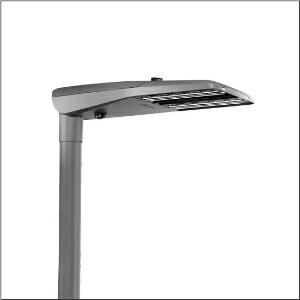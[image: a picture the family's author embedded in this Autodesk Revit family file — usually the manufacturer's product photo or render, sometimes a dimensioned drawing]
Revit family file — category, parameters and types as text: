
# Revit family: streetlight_sl_11_iq_midi___st1_2a_5xc3a11y08me_f942
name_source: partatom
category: Lighting Fixtures
units: mm (PartAtom-declared; Revit-internal decimal feet)

## family parameters
Cut with Voids When Loaded = No
Host = Face
Light Source = No
Part Type = Normal
Room Calculation Point = No
Round Connector Dimension = Use Diameter
Shared = No

## types (1)
- --- (1 x LED, 11200 lm, 123.4 W, 1800K)
    Apparent Load = 123 VA
    CIE Flux Codes = 32 70 96 100 100
    Color Rendering = 70
    Color Temperature = 1800K
    Default Elevation = 1800 mm  [stored 5.90551 ft]
    Description = Streetlight SL 11 iQ midi, mast luminaire, primary light control with 3 zone facetted reflector, of plastic, silver coated, highly specular, primary optical cover: cover, of PMMA, transparent, light distribution: ST1.2a, light emission: direct distribution, primary light characteristic: asymmetric, installation type: post-top, side-entry, LED, High Power LED, rated luminous flux: 11.200lm, luminous efficacy: 91lm/W, light colour: 718, colour temperature: 1800K, control: presetting dimming logarithmic, Street-Remote, Auto-Match, Temp-Guard, Lumen-Switch, Night-Set, Smart-Wire, Light-Fading, Desk-Remote (wireless, voltage-free reading and setting of iQ features in the workshop via application-optimized NFC function/RFID function), optimised constant luminous flux control (CLO 2.0), with cable H07RN-F 5x 1.5mm², mains connection: 230..240V, AC, 50/60Hz, connection cable pre-assembled, cable length: 12,5m, start of lifetime: 123W, end of service life: 131W, reduction: 54W, luminaire housing, of diecast aluminium, powder-coated, Siteco® metallic grey (DB 702S), please order mast flange separately, inclination adjustable without tools: 0°, 5°, 10°, 15° (post-top) | 0°, -5°, -10°, -15° (side-entry), sealing non-destructively replaceable, multi-level sealing system, length: 780mm, width: 376mm, height: 118mm, mast flange for spigot size: 42mm (side-entry): 5XC10008XM4, 60/48mm (side-entry/post-top): 5XC10108XM2, 76/60mm (side-entry/post-top): 5XC10108XM1, equipment: Power, Smart Interface below and above, protection rating (complete): IP66, insulation class (complete): insulation class II (safety insulation), certification: CE, ENEC, VDE, UKCA, impact resistance: IK09, permissible operating ambient temperature for outdoor applications: -25..+50°C, standard-compliant lighting for roads and squares, Environmental Product Declaration (EPD) tested and certified by an independent institute, packaging unit: 1 piece

Light Distribution: ST1.2a
    Height = 118 mm
    Lamp = 1 x LED
    Lamp Light Flux = 11200 lm
    Lamp Power = 123.4 W
    Lamp count = 1
    Length = 780 mm
    Luminous efficacy = 91 lm/W
    Manufacturer = Siteco
    ModVariant = No
    Model = 5XC3A11Y08ME
    Number of Poles = 1
    OnlyDefault = Yes
    Power Factor = 1
    Product Name = Streetlight SL 11 iQ midi | ST1.2a
    Product group = mast luminaire | pylon top
    ProductGroupID = 6100
    Protection Class = Protection class II
    Protection Degree = IP 66
    RLX_Detail_Level = 1
    RLX_Emergency_Light_Flux = 0 lm
    RLX_Emergency_Type = 0
    RLX_Emergency_Type_DB = No
    RlxData = <blob elided: 69609 chars, md5=4086d98f>
    Socket = socket
    Standby Power = 0 W
    System Light Flux = 11200 lm
    System Power = 123 W
    Type Comments = factory setting: luminous flux: 100 % | dim-lin: 254 | 553 mA
    Type Image = l_1004429.jpg
    URL = http://relux.com
    VarID = @adj_002883
    Voltage = 0 V
    Weight = 0.00 kg
    Width = 376 mm

note: [stored X ft] marks values corroborated as IEEE doubles in the binary element streams (Revit-internal decimal feet)

## geometry (parser evidence)
native form markers: Blend x4, Sweep x10
no freeform markers — native parametric forms only
